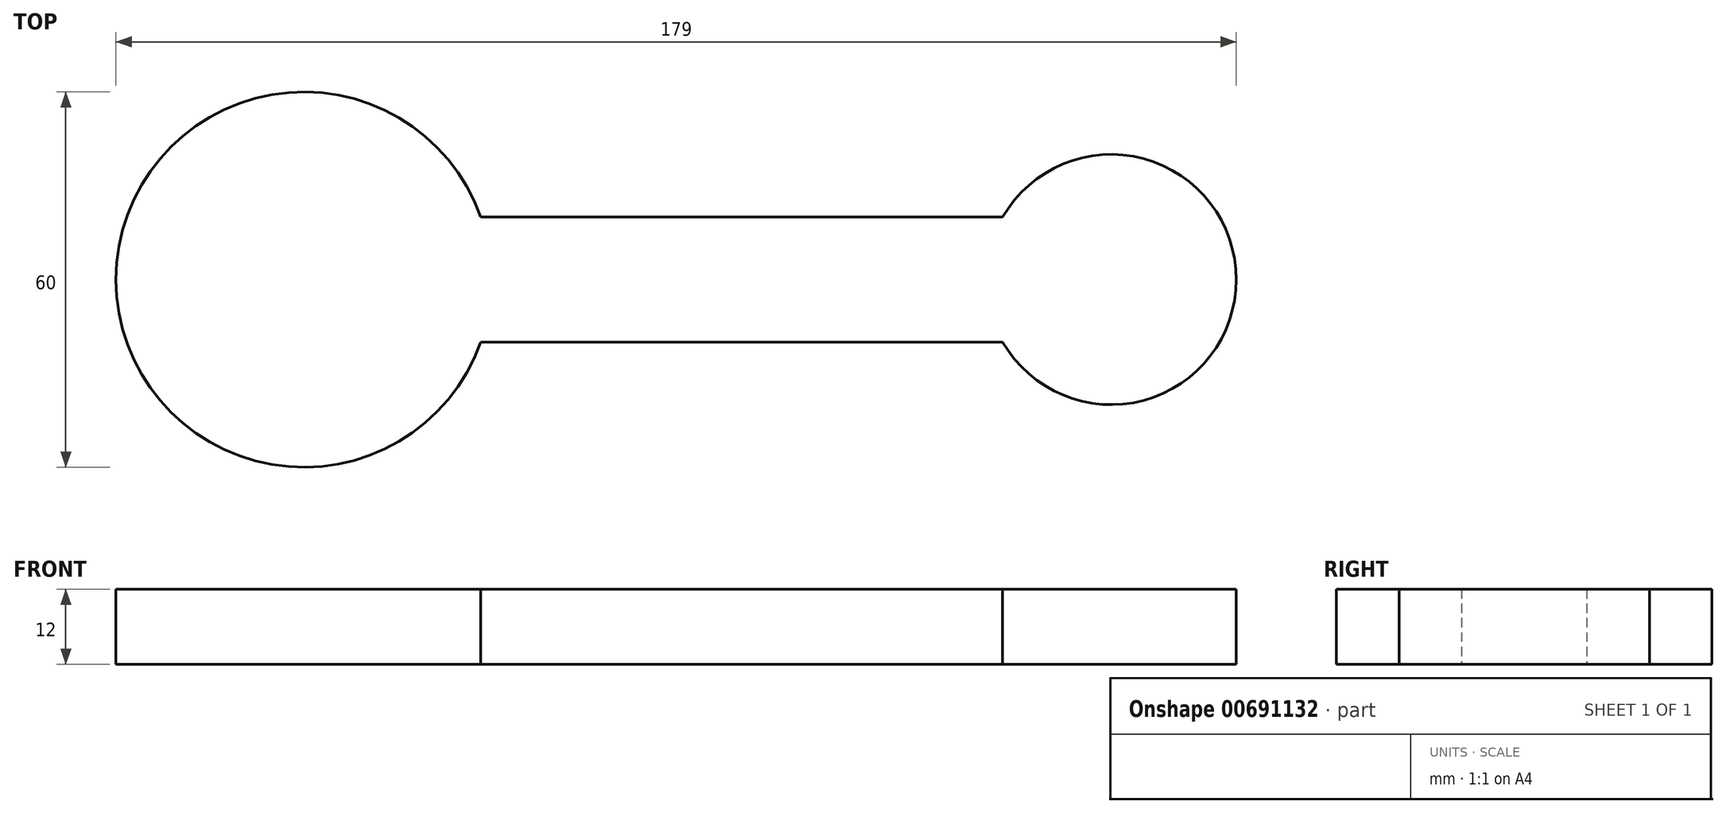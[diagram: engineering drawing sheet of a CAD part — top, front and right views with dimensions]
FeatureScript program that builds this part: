
annotation { "Feature Type Name" : "Feature", "Feature Type Description" : "" }
export const myFeature = defineFeature(function(context is Context, id is Id, definition is map)
    precondition{}
    {
        {
            var Q0;
            Q0=qCreatedBy(makeId("Top.planeOp"),FACE);
            var sketch = newSketch(context, id + "F0", { "sketchPlane" : qUnion([Q0])});
            skLineSegment(sketch, "E0.bottom", {"start": v(-64.5, -10) * mm, "end": v(64.5, -10) * mm});
            skLineSegment(sketch, "E0.top", {"start": v(-64.5, 10) * mm, "end": v(64.5, 10) * mm});
            skLineSegment(sketch, "E0.left", {"start": v(-64.5, -10) * mm, "end": v(-64.5, 10) * mm});
            skLineSegment(sketch, "E0.right", {"start": v(64.5, -10) * mm, "end": v(64.5, 10) * mm});
            skPoint(sketch, "E0.middle", {"position": v(0, 0) * mm});
            skCircle(sketch, "E1", {"center": v(-64.5, 0) * mm, "radius": 30 * mm});
            skCircle(sketch, "E2.MirrorC", {"center": v(64.5, 0) * mm, "radius": 20 * mm});
            skSolve(sketch);
        }
        {
            var Q0;
            Q0 = qSketchRegion(id + "F0", true);
            extrude(context, id + "F1", {"entities" : qUnion([Q0]), "depth" : 12 * mm, "offsetDistance" : 25 * mm});
        }
    });
